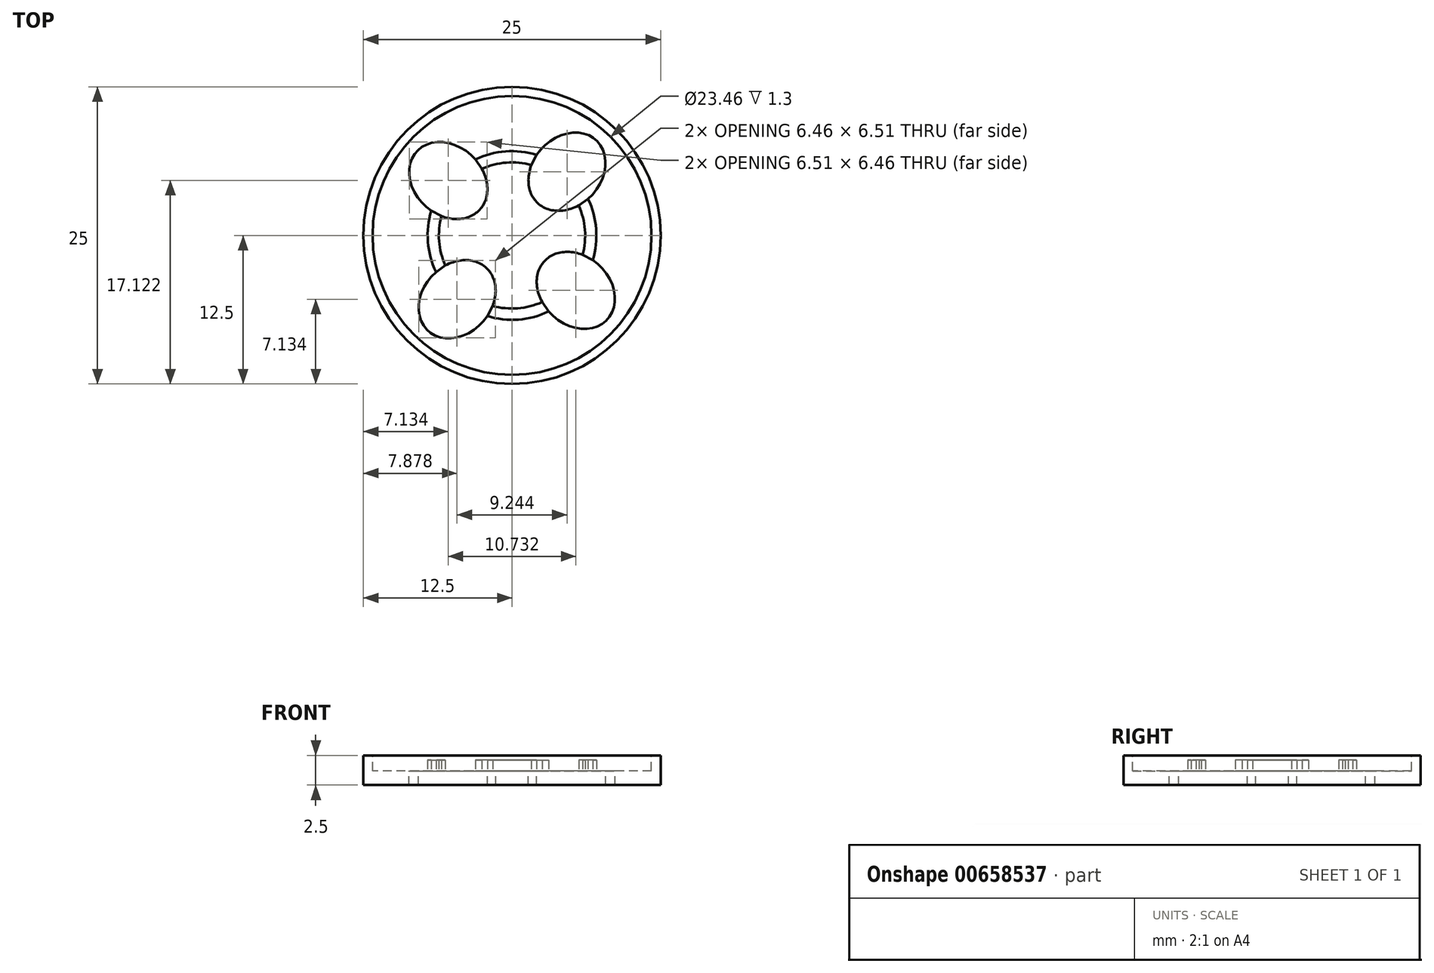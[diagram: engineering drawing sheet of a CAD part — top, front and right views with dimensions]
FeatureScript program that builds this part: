
annotation { "Feature Type Name" : "Feature", "Feature Type Description" : "" }
export const myFeature = defineFeature(function(context is Context, id is Id, definition is map)
    precondition{}
    {
        {
            var Q0;
            Q0=qCreatedBy(makeId("Top.planeOp"),FACE);
            var sketch = newSketch(context, id + "F0", { "sketchPlane" : qUnion([Q0])});
            skCircle(sketch, "E0", {"center": v(0, 0) * mm, "radius": 12.5 * mm});
            skEllipse(sketch, "E1", {"center": v(-5.37, 4.62) * mm, "majorRadius": 3.6 * mm, "minorRadius": 2.88 * mm, "majorAxis": v(0.73, -0.68)});
            skEllipse(sketch, "E2.1.0", {"center": v(4.62, 5.37) * mm, "majorRadius": 3.6 * mm, "minorRadius": 2.88 * mm, "majorAxis": v(-0.68, -0.73)});
            skEllipse(sketch, "E2.2.0", {"center": v(5.37, -4.62) * mm, "majorRadius": 3.6 * mm, "minorRadius": 2.88 * mm, "majorAxis": v(-0.73, 0.68)});
            skEllipse(sketch, "E2.3.0", {"center": v(-4.62, -5.37) * mm, "majorRadius": 3.6 * mm, "minorRadius": 2.88 * mm, "majorAxis": v(0.68, 0.73)});
            skLineSegment(sketch, "E2.anchor1", {"start": v(0, 0) * mm, "end": v(-5.37, 4.62) * mm, "construction": true});
            skLineSegment(sketch, "E2.anchor2", {"start": v(0, 0) * mm, "end": v(-4.62, -5.37) * mm, "construction": true});
            skSolve(sketch);
        }
        {
            var Q0;
            Q0=makeQuery(id+"F0.imprint","IMPRINT",FACE,{"disambiguationData":[TD([[makeQuery(id+"F0.imprint","IMPRINT",EDGE,{"derivedFrom":sQuery(id+"F0.wireOp",EDGE,"E0")}),1.0]])]});
            extrude(context, id + "F1", {"entities" : qUnion([Q0]), "depth" : 2.5 * mm, "offsetDistance" : 25.4 * mm});
        }
        {
            var Q0;
            Q0=makeQuery(id+"F1.opExtrude","CAP_FACE",FACE,{"disambiguationData":[OSD([sQuery(id+"F0.wireOp",EDGE,"E0"),sQuery(id+"F0.wireOp",EDGE,"E1"),sQuery(id+"F0.wireOp",EDGE,"E2.1.0"),sQuery(id+"F0.wireOp",EDGE,"E2.2.0"),sQuery(id+"F0.wireOp",EDGE,"E2.3.0")])],"isStart":false});
            var sketch = newSketch(context, id + "F2", { "sketchPlane" : qUnion([Q0])});
            skCircle(sketch, "E3", {"center": v(0, 0) * mm, "radius": 12.46 * mm});
            skCircle(sketch, "E4", {"center": v(0, 0) * mm, "radius": 11.73 * mm});
            skSolve(sketch);
        }
        {
            var Q0;
            Q0=makeQuery(id+"F2.imprint","IMPRINT",FACE,{"disambiguationData":[TD([[makeQuery(id+"F2.imprint","IMPRINT",EDGE,{"derivedFrom":sQuery(id+"F2.wireOp",EDGE,"E4")}),1.0]])]});
            extrude(context, id + "F3", {"entities" : qUnion([Q0]), "operationType" : NewBodyOperationType.REMOVE, "oppositeDirection" : true, "depth" : 1.3 * mm, "offsetDistance" : 25.4 * mm});
        }
        {
            var Q0;
            Q0=makeQuery(id+"F3.boolean.opBoolean","COPY",FACE,{"derivedFrom":makeQuery(id+"F3.opExtrude","CAP_FACE",FACE,{"disambiguationData":[OSD([sQuery(id+"F0.wireOp",EDGE,"E1"),sQuery(id+"F0.wireOp",EDGE,"E2.1.0"),sQuery(id+"F0.wireOp",EDGE,"E2.2.0"),sQuery(id+"F0.wireOp",EDGE,"E2.3.0"),sQuery(id+"F2.wireOp",EDGE,"E4")])],"isStart":false})});
            var sketch = newSketch(context, id + "F4", { "sketchPlane" : qUnion([Q0])});
            skArc(sketch, "E5", {"start": v(-6.79, 2.08) * mm, "mid": v(-7.08, -0.54) * mm, "end": v(-6.4, -3.08) * mm});
            skPoint(sketch, "E6", {"position": v(-6.79, 2.08) * mm});
            skPoint(sketch, "E7", {"position": v(-3.08, 6.4) * mm});
            skPoint(sketch, "E8", {"position": v(-2.53, 5.6) * mm});
            skPoint(sketch, "E9", {"position": v(-5.93, 1.63) * mm});
            skPoint(sketch, "E10", {"position": v(2.08, 6.79) * mm});
            skPoint(sketch, "E11", {"position": v(6.4, 3.08) * mm});
            skPoint(sketch, "E12", {"position": v(1.63, 5.93) * mm});
            skPoint(sketch, "E13", {"position": v(5.6, 2.53) * mm});
            skPoint(sketch, "E14", {"position": v(5.93, -1.63) * mm});
            skPoint(sketch, "E15", {"position": v(2.53, -5.6) * mm});
            skPoint(sketch, "E16", {"position": v(6.79, -2.08) * mm});
            skPoint(sketch, "E17", {"position": v(3.08, -6.4) * mm});
            skPoint(sketch, "E18", {"position": v(-2.08, -6.79) * mm});
            skPoint(sketch, "E19", {"position": v(-6.4, -3.08) * mm});
            skPoint(sketch, "E20", {"position": v(-5.6, -2.53) * mm});
            skPoint(sketch, "E21", {"position": v(-1.63, -5.93) * mm});
            skArc(sketch, "E22.trimOffspring", {"start": v(-5.93, 1.63) * mm, "mid": v(-6.13, -0.48) * mm, "end": v(-5.6, -2.53) * mm});
            skArc(sketch, "E23.trimOffspring", {"start": v(2.08, 6.79) * mm, "mid": v(-0.54, 7.08) * mm, "end": v(-3.08, 6.4) * mm});
            skArc(sketch, "E24.trimOffspring", {"start": v(1.63, 5.93) * mm, "mid": v(-0.48, 6.13) * mm, "end": v(-2.53, 5.6) * mm});
            skArc(sketch, "E25.trimOffspring", {"start": v(5.93, -1.63) * mm, "mid": v(6.13, 0.48) * mm, "end": v(5.6, 2.53) * mm});
            skArc(sketch, "E26.trimOffspring", {"start": v(6.79, -2.08) * mm, "mid": v(7.08, 0.54) * mm, "end": v(6.4, 3.08) * mm});
            skArc(sketch, "E27.trimOffspring", {"start": v(-1.63, -5.93) * mm, "mid": v(0.48, -6.13) * mm, "end": v(2.53, -5.6) * mm});
            skArc(sketch, "E28.trimOffspring", {"start": v(-2.08, -6.79) * mm, "mid": v(0.54, -7.08) * mm, "end": v(3.08, -6.4) * mm});
            skLineSegment(sketch, "E29", {"start": v(-6.79, 2.08) * mm, "end": v(-5.93, 1.63) * mm});
            skLineSegment(sketch, "E30", {"start": v(-5.6, -2.53) * mm, "end": v(-6.4, -3.08) * mm});
            skLineSegment(sketch, "E31", {"start": v(-1.63, -5.93) * mm, "end": v(-2.08, -6.79) * mm});
            skLineSegment(sketch, "E32", {"start": v(2.53, -5.6) * mm, "end": v(3.08, -6.4) * mm});
            skLineSegment(sketch, "E33", {"start": v(6.79, -2.08) * mm, "end": v(5.93, -1.63) * mm});
            skLineSegment(sketch, "E34", {"start": v(6.4, 3.08) * mm, "end": v(5.6, 2.53) * mm});
            skLineSegment(sketch, "E35", {"start": v(2.08, 6.79) * mm, "end": v(1.63, 5.93) * mm});
            skLineSegment(sketch, "E36", {"start": v(-3.08, 6.4) * mm, "end": v(-2.53, 5.6) * mm});
            skSolve(sketch);
        }
        {
            var Q0;
            Q0 = qSketchRegion(id + "F4", true);
            extrude(context, id + "F5", {"entities" : qUnion([Q0]), "depth" : .9 * mm, "offsetDistance" : 25.4 * mm});
        }
        {
            var Q0;
            Q0 = qSketchRegion(id + "F4", true);
            extrude(context, id + "F6", {"entities" : qUnion([Q0]), "depth" : .9 * mm, "offsetDistance" : 25.4 * mm});
        }
    });
